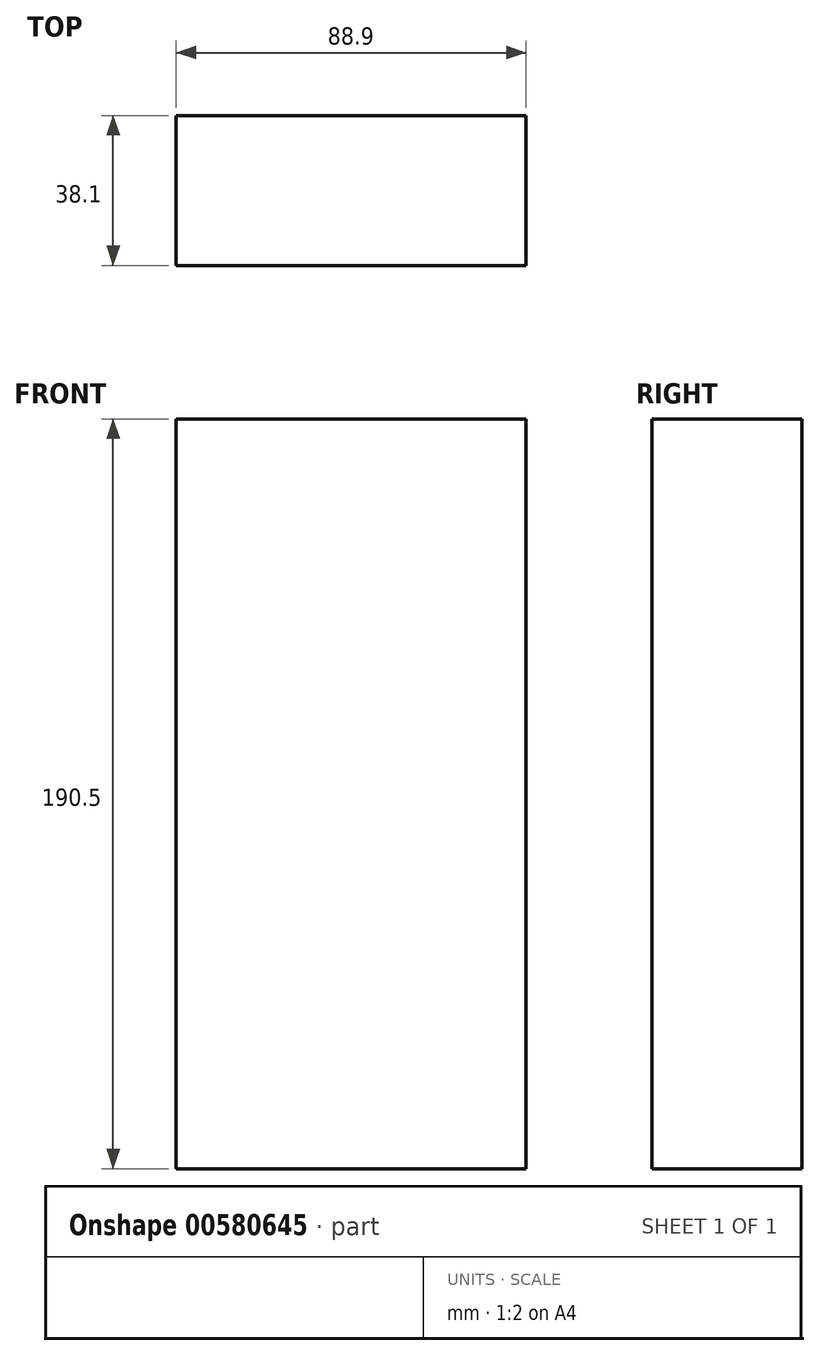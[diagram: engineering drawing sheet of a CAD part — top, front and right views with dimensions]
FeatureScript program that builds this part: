
annotation { "Feature Type Name" : "Feature", "Feature Type Description" : "" }
export const myFeature = defineFeature(function(context is Context, id is Id, definition is map)
    precondition{}
    {
        {
            var Q0;
            Q0=qCreatedBy(makeId("Top.planeOp"),FACE);
            var sketch = newSketch(context, id + "F0", { "sketchPlane" : qUnion([Q0])});
            skLineSegment(sketch, "E0.bottom", {"start": v(44.45, -19.05) * mm, "end": v(-44.45, -19.05) * mm});
            skLineSegment(sketch, "E0.top", {"start": v(44.45, 19.05) * mm, "end": v(-44.45, 19.05) * mm});
            skLineSegment(sketch, "E0.left", {"start": v(44.45, -19.05) * mm, "end": v(44.45, 19.05) * mm});
            skLineSegment(sketch, "E0.right", {"start": v(-44.45, -19.05) * mm, "end": v(-44.45, 19.05) * mm});
            skPoint(sketch, "E0.middle", {"position": v(0, 0) * mm});
            skSolve(sketch);
        }
        {
            var Q0;
            Q0=makeQuery(id+"F0.imprint","IMPRINT",FACE,{"disambiguationData":[TD([[makeQuery(id+"F0.imprint","IMPRINT",EDGE,{"derivedFrom":sQuery(id+"F0.wireOp",EDGE,"E0.bottom")}),-1.0]])]});
            extrude(context, id + "F1", {"entities" : qUnion([Q0]), "depth" : 190.5 * mm, "offsetDistance" : 25.4 * mm});
        }
    });
